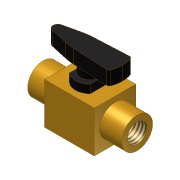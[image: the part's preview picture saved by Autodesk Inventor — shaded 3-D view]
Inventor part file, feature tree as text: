
AUTODESK INVENTOR PART (.ipt)
format: ipt  version: 2014 SP1 (Build 180222100, 222)  size: 166,912 bytes
history: native  units: mm (DEFAULTED — no unit token found)
features: extrude x10, sketch x10, projected_geometry x5, thread x2
ambient origin geometry x8: Origin, YZ Plane, XZ Plane, XY Plane, X Axis, Y Axis, Z Axis, Center Point
bodies: Solid1 (feature_tree)
feature tree (27):
  extrude  "Extrusion1"  Depth=22.86mm
  extrude  "Extrusion2"  Depth=19.05mm
  extrude  "Extrusion3"  Depth=10.16mm
  extrude  "Extrusion4"  Depth=3.81mm TaperAngle=0.0deg
  extrude  "Extrusion5"  Depth=6.35mm TaperAngle=0.0deg
  extrude  "Extrusion6"  Depth=9.525mm TaperAngle=0.0deg
  extrude  "Extrusion7"  Depth=9.525mm
  extrude  "Extrusion9"  Depth=1.6002mm TaperAngle=0.0deg
  thread  "Thread1"  [1 undecoded]
  thread  "Thread2"  [1 undecoded]
  extrude  "Extrusion10"  [1 undecoded]
  sketch  "Sketch1"  dims[d0=19.05mm d1=22.86mm]
  sketch  "Sketch2"  dims[d2=19.05mm d3=0.0mm d4=14.224mm]
  projected_geometry  "Projected Loop1"
  sketch  "Sketch3"  dims[d5=10.16mm d6=0.0mm d7=14.224mm]
  projected_geometry  "Projected Loop2"
  sketch  "Sketch4"  dims[d8=10.16mm d9=0.0mm d10=3.81mm d11=0.0mm]
  projected_geometry  "Projected Loop3"
  sketch  "Sketch5"  dims[d12=10.16mm d13=0.0mm d14=6.35mm d15=0.0mm]
  projected_geometry  "Projected Loop4"
  sketch  "Sketch6"  dims[d16=8.89mm d17=9.525mm d18=0.0mm]
  projected_geometry  "Projected Loop5"
  sketch  "Sketch7"  dims[d19=8.89mm d21=0.0mm d22=9.525mm d23=3.175mm]
  sketch  "Sketch8"  dims[d24=71.4502mm d25=0.0mm d26=25.4mm d27=0.0mm d28=25.4mm d29=0.0mm d30=1.6002mm d31=0.0mm]
  sketch  "Sketch9"
  sketch  "Sketch10"
  extrude  "Extrusion8"  [1 undecoded]
note: 4 required parameter values undecoded (feature->parameter linkage not recoverable at this tier; creation-order binding heuristic only, values carry confidence <= 0.55)
